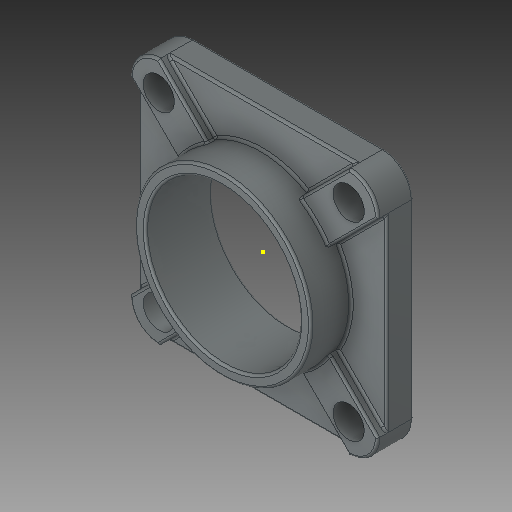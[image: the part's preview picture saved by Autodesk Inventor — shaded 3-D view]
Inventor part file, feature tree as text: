
AUTODESK INVENTOR PART (.ipt)
format: ipt  version: 2019 (Build 230136000, 136)  size: 484,864 bytes
history: native  units: in
note: dims shown in document units (in); Inventor stores cm internally (conversion verified against a paired STEP export)
features: sketch x10, other x3
ambient origin geometry x8: Origin, YZ Plane, XZ Plane, XY Plane, X Axis, Y Axis, Z Axis, Center Point
bodies: Solid1 (feature_tree)
feature tree (13):
  other  "project flange bearing part1_MIR3.ipt"
  other  "Solid1::project flange bearing part1_MIR3.ipt"
  other  "TaggingFeature1"
  sketch  "Sketch1"  dims[d0=0.3937in]
  sketch  "Sketch2"
  sketch  "Sketch3"
  sketch  "Sketch4"
  sketch  "Sketch5"
  sketch  "Sketch6"
  sketch  "Sketch7"
  sketch  "Sketch8"
  sketch  "Sketch9"
  sketch  "Sketch10"
